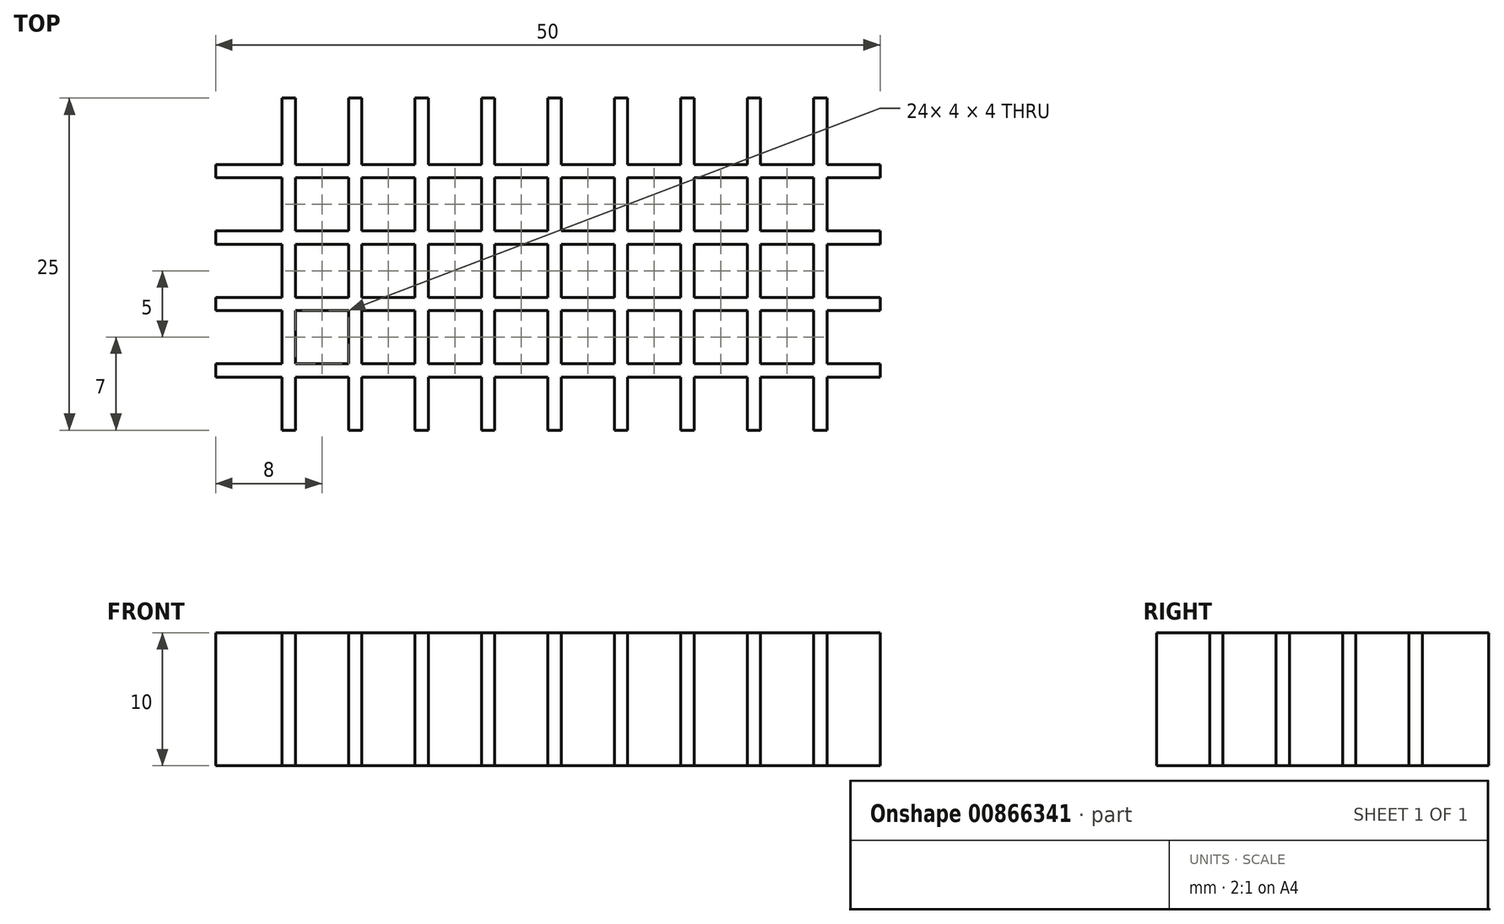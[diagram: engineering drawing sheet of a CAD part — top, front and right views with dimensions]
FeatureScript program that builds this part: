
annotation { "Feature Type Name" : "Feature", "Feature Type Description" : "" }
export const myFeature = defineFeature(function(context is Context, id is Id, definition is map)
    precondition{}
    {
        {
            var Q0;
            Q0=qCreatedBy(makeId("Top.planeOp"),FACE);
            var sketch = newSketch(context, id + "F0", { "sketchPlane" : qUnion([Q0])});
            skLineSegment(sketch, "E0.bottom", {"start": v(0, 0) * mm, "end": v(50, 0) * mm, "construction": true});
            skLineSegment(sketch, "E0.top", {"start": v(0, 25) * mm, "end": v(50, 25) * mm, "construction": true});
            skLineSegment(sketch, "E0.left", {"start": v(0, 0) * mm, "end": v(0, 4) * mm, "construction": true});
            skLineSegment(sketch, "E0.right", {"start": v(50, 0) * mm, "end": v(50, 25) * mm, "construction": true});
            skLineSegment(sketch, "E1", {"start": v(0, 0) * mm, "end": v(0, 25) * mm});
            skLineSegment(sketch, "E2", {"start": v(0, 25) * mm, "end": v(1, 25) * mm});
            skLineSegment(sketch, "E3", {"start": v(1, 24) * mm, "end": v(1, 20) * mm});
            skLineSegment(sketch, "E4", {"start": v(1, 0) * mm, "end": v(0, 0) * mm});
            skLineSegment(sketch, "E5.1.0.0", {"start": v(5, 0) * mm, "end": v(5, 4) * mm});
            skLineSegment(sketch, "E5.1.0.1", {"start": v(6, 24) * mm, "end": v(6, 20) * mm});
            skLineSegment(sketch, "E5.1.0.2", {"start": v(6, 0) * mm, "end": v(5, 0) * mm});
            skLineSegment(sketch, "E5.1.0.3", {"start": v(5, 25) * mm, "end": v(6, 25) * mm});
            skLineSegment(sketch, "E5.2.0.0", {"start": v(10, 0) * mm, "end": v(10, 4) * mm});
            skLineSegment(sketch, "E5.2.0.1", {"start": v(11, 24) * mm, "end": v(11, 20) * mm});
            skLineSegment(sketch, "E5.2.0.2", {"start": v(11, 0) * mm, "end": v(10, 0) * mm});
            skLineSegment(sketch, "E5.2.0.3", {"start": v(10, 25) * mm, "end": v(11, 25) * mm});
            skLineSegment(sketch, "E5.3.0.0", {"start": v(15, 0) * mm, "end": v(15, 4) * mm});
            skLineSegment(sketch, "E5.3.0.1", {"start": v(16, 24) * mm, "end": v(16, 20) * mm});
            skLineSegment(sketch, "E5.3.0.2", {"start": v(16, 0) * mm, "end": v(15, 0) * mm});
            skLineSegment(sketch, "E5.3.0.3", {"start": v(15, 25) * mm, "end": v(16, 25) * mm});
            skLineSegment(sketch, "E5.4.0.0", {"start": v(20, 0) * mm, "end": v(20, 4) * mm});
            skLineSegment(sketch, "E5.4.0.1", {"start": v(21, 24) * mm, "end": v(21, 20) * mm});
            skLineSegment(sketch, "E5.4.0.2", {"start": v(21, 0) * mm, "end": v(20, 0) * mm});
            skLineSegment(sketch, "E5.4.0.3", {"start": v(20, 25) * mm, "end": v(21, 25) * mm});
            skLineSegment(sketch, "E5.5.0.0", {"start": v(25, 0) * mm, "end": v(25, 4) * mm});
            skLineSegment(sketch, "E5.5.0.1", {"start": v(26, 24) * mm, "end": v(26, 20) * mm});
            skLineSegment(sketch, "E5.5.0.2", {"start": v(26, 0) * mm, "end": v(25, 0) * mm});
            skLineSegment(sketch, "E5.5.0.3", {"start": v(25, 25) * mm, "end": v(26, 25) * mm});
            skLineSegment(sketch, "E5.6.0.0", {"start": v(30, 0) * mm, "end": v(30, 4) * mm});
            skLineSegment(sketch, "E5.6.0.1", {"start": v(31, 24) * mm, "end": v(31, 20) * mm});
            skLineSegment(sketch, "E5.6.0.2", {"start": v(31, 0) * mm, "end": v(30, 0) * mm});
            skLineSegment(sketch, "E5.6.0.3", {"start": v(30, 25) * mm, "end": v(31, 25) * mm});
            skLineSegment(sketch, "E5.7.0.0", {"start": v(35, 0) * mm, "end": v(35, 4) * mm});
            skLineSegment(sketch, "E5.7.0.1", {"start": v(36, 24) * mm, "end": v(36, 20) * mm});
            skLineSegment(sketch, "E5.7.0.2", {"start": v(36, 0) * mm, "end": v(35, 0) * mm});
            skLineSegment(sketch, "E5.7.0.3", {"start": v(35, 25) * mm, "end": v(36, 25) * mm});
            skLineSegment(sketch, "E5.8.0.0", {"start": v(40, 0) * mm, "end": v(40, 4) * mm});
            skLineSegment(sketch, "E5.8.0.1", {"start": v(41, 24) * mm, "end": v(41, 20) * mm});
            skLineSegment(sketch, "E5.8.0.2", {"start": v(41, 0) * mm, "end": v(40, 0) * mm});
            skLineSegment(sketch, "E5.8.0.3", {"start": v(40, 25) * mm, "end": v(41, 25) * mm});
            skLineSegment(sketch, "E5.9.0.0", {"start": v(45, 0) * mm, "end": v(45, 4) * mm});
            skLineSegment(sketch, "E5.9.0.1", {"start": v(46, 24) * mm, "end": v(46, 20) * mm});
            skLineSegment(sketch, "E5.9.0.2", {"start": v(46, 0) * mm, "end": v(45, 0) * mm});
            skLineSegment(sketch, "E5.9.0.3", {"start": v(45, 25) * mm, "end": v(46, 25) * mm});
            skLineSegment(sketch, "E5.direction1", {"start": v(0, 0) * mm, "end": v(5, 0) * mm, "construction": true});
            skLineSegment(sketch, "E6", {"start": v(0, 25) * mm, "end": v(50, 25) * mm});
            skLineSegment(sketch, "E7", {"start": v(50, 25) * mm, "end": v(50, 24) * mm});
            skLineSegment(sketch, "E8", {"start": v(50, 24) * mm, "end": v(46, 24) * mm});
            skLineSegment(sketch, "E9", {"start": v(0, 24) * mm, "end": v(0, 25) * mm});
            skLineSegment(sketch, "E10.1.0.0", {"start": v(50, 19) * mm, "end": v(46, 19) * mm});
            skLineSegment(sketch, "E10.1.0.1", {"start": v(1, 20) * mm, "end": v(5, 20) * mm});
            skLineSegment(sketch, "E10.1.0.2", {"start": v(0, 19) * mm, "end": v(0, 20) * mm});
            skLineSegment(sketch, "E10.1.0.3", {"start": v(50, 20) * mm, "end": v(50, 19) * mm});
            skLineSegment(sketch, "E10.2.0.0", {"start": v(50, 14) * mm, "end": v(46, 14) * mm});
            skLineSegment(sketch, "E10.2.0.1", {"start": v(1, 15) * mm, "end": v(5, 15) * mm});
            skLineSegment(sketch, "E10.2.0.2", {"start": v(0, 14) * mm, "end": v(0, 15) * mm});
            skLineSegment(sketch, "E10.2.0.3", {"start": v(50, 15) * mm, "end": v(50, 14) * mm});
            skLineSegment(sketch, "E10.3.0.0", {"start": v(50, 9) * mm, "end": v(46, 9) * mm});
            skLineSegment(sketch, "E10.3.0.1", {"start": v(1, 10) * mm, "end": v(5, 10) * mm});
            skLineSegment(sketch, "E10.3.0.2", {"start": v(0, 9) * mm, "end": v(0, 10) * mm});
            skLineSegment(sketch, "E10.3.0.3", {"start": v(50, 10) * mm, "end": v(50, 9) * mm});
            skLineSegment(sketch, "E10.4.0.0", {"start": v(50, 4) * mm, "end": v(46, 4) * mm});
            skLineSegment(sketch, "E10.4.0.1", {"start": v(1, 5) * mm, "end": v(5, 5) * mm});
            skLineSegment(sketch, "E10.4.0.2", {"start": v(0, 4) * mm, "end": v(0, 5) * mm});
            skLineSegment(sketch, "E10.4.0.3", {"start": v(50, 5) * mm, "end": v(50, 4) * mm});
            skLineSegment(sketch, "E10.direction1", {"start": v(0, 24) * mm, "end": v(0, 19) * mm, "construction": true});
            skLineSegment(sketch, "E11.trimOffspring", {"start": v(5, 5) * mm, "end": v(5, 9) * mm});
            skLineSegment(sketch, "E12.trimOffspring", {"start": v(6, 5) * mm, "end": v(10, 5) * mm});
            skLineSegment(sketch, "E13.trimOffspring", {"start": v(6, 4) * mm, "end": v(6, 0) * mm});
            skLineSegment(sketch, "E14.trimOffspring", {"start": v(5, 4) * mm, "end": v(1, 4) * mm});
            skLineSegment(sketch, "E15.trimOffspring", {"start": v(1, 4) * mm, "end": v(1, 0) * mm});
            skPoint(sketch, "E16.orphan", {"position": v(0, 5) * mm});
            skPoint(sketch, "E17.orphan", {"position": v(0, 10) * mm});
            skPoint(sketch, "E18.orphan", {"position": v(0, 15) * mm});
            skPoint(sketch, "E19.orphan", {"position": v(0, 20) * mm});
            skLineSegment(sketch, "E20.trimOffspring", {"start": v(46, 20) * mm, "end": v(50, 20) * mm});
            skLineSegment(sketch, "E21.trimOffspring", {"start": v(45, 19) * mm, "end": v(41, 19) * mm});
            skLineSegment(sketch, "E22.trimOffspring", {"start": v(45, 20) * mm, "end": v(45, 24) * mm});
            skLineSegment(sketch, "E23.trimOffspring", {"start": v(46, 19) * mm, "end": v(46, 15) * mm});
            skLineSegment(sketch, "E24.trimOffspring", {"start": v(46, 15) * mm, "end": v(50, 15) * mm});
            skLineSegment(sketch, "E25.trimOffspring", {"start": v(45, 14) * mm, "end": v(41, 14) * mm});
            skLineSegment(sketch, "E26.trimOffspring", {"start": v(45, 15) * mm, "end": v(45, 19) * mm});
            skLineSegment(sketch, "E27.trimOffspring", {"start": v(46, 14) * mm, "end": v(46, 10) * mm});
            skLineSegment(sketch, "E28.trimOffspring", {"start": v(46, 10) * mm, "end": v(50, 10) * mm});
            skLineSegment(sketch, "E29.trimOffspring", {"start": v(46, 9) * mm, "end": v(46, 5) * mm});
            skLineSegment(sketch, "E30.trimOffspring", {"start": v(45, 9) * mm, "end": v(41, 9) * mm});
            skLineSegment(sketch, "E31.trimOffspring", {"start": v(45, 10) * mm, "end": v(45, 14) * mm});
            skLineSegment(sketch, "E32.trimOffspring", {"start": v(46, 5) * mm, "end": v(50, 5) * mm});
            skLineSegment(sketch, "E33.trimOffspring", {"start": v(46, 4) * mm, "end": v(46, 0) * mm});
            skLineSegment(sketch, "E34.trimOffspring", {"start": v(45, 4) * mm, "end": v(41, 4) * mm});
            skLineSegment(sketch, "E35.trimOffspring", {"start": v(45, 5) * mm, "end": v(45, 9) * mm});
            skLineSegment(sketch, "E36.trimOffspring", {"start": v(40, 5) * mm, "end": v(40, 9) * mm});
            skLineSegment(sketch, "E37.trimOffspring", {"start": v(41, 5) * mm, "end": v(45, 5) * mm});
            skLineSegment(sketch, "E38.trimOffspring", {"start": v(41, 4) * mm, "end": v(41, 0) * mm});
            skLineSegment(sketch, "E39.trimOffspring", {"start": v(40, 4) * mm, "end": v(36, 4) * mm});
            skLineSegment(sketch, "E40.trimOffspring", {"start": v(36, 5) * mm, "end": v(40, 5) * mm});
            skLineSegment(sketch, "E41.trimOffspring", {"start": v(36, 4) * mm, "end": v(36, 0) * mm});
            skLineSegment(sketch, "E42.trimOffspring", {"start": v(35, 4) * mm, "end": v(31, 4) * mm});
            skLineSegment(sketch, "E43.trimOffspring", {"start": v(35, 5) * mm, "end": v(35, 9) * mm});
            skLineSegment(sketch, "E44.trimOffspring", {"start": v(35, 9) * mm, "end": v(31, 9) * mm});
            skLineSegment(sketch, "E45.trimOffspring", {"start": v(35, 10) * mm, "end": v(35, 14) * mm});
            skLineSegment(sketch, "E46.trimOffspring", {"start": v(36, 10) * mm, "end": v(40, 10) * mm});
            skLineSegment(sketch, "E47.trimOffspring", {"start": v(36, 9) * mm, "end": v(36, 5) * mm});
            skLineSegment(sketch, "E48.trimOffspring", {"start": v(40, 10) * mm, "end": v(40, 14) * mm});
            skLineSegment(sketch, "E49.trimOffspring", {"start": v(41, 10) * mm, "end": v(45, 10) * mm});
            skLineSegment(sketch, "E50.trimOffspring", {"start": v(41, 9) * mm, "end": v(41, 5) * mm});
            skLineSegment(sketch, "E51.trimOffspring", {"start": v(40, 9) * mm, "end": v(36, 9) * mm});
            skLineSegment(sketch, "E52.trimOffspring", {"start": v(40, 14) * mm, "end": v(36, 14) * mm});
            skLineSegment(sketch, "E53.trimOffspring", {"start": v(41, 15) * mm, "end": v(45, 15) * mm});
            skLineSegment(sketch, "E54.trimOffspring", {"start": v(40, 15) * mm, "end": v(40, 19) * mm});
            skLineSegment(sketch, "E55.trimOffspring", {"start": v(41, 14) * mm, "end": v(41, 10) * mm});
            skLineSegment(sketch, "E56.trimOffspring", {"start": v(40, 19) * mm, "end": v(36, 19) * mm});
            skLineSegment(sketch, "E57.trimOffspring", {"start": v(41, 20) * mm, "end": v(45, 20) * mm});
            skLineSegment(sketch, "E58.trimOffspring", {"start": v(40, 20) * mm, "end": v(40, 24) * mm});
            skLineSegment(sketch, "E59.trimOffspring", {"start": v(41, 19) * mm, "end": v(41, 15) * mm});
            skLineSegment(sketch, "E60.trimOffspring", {"start": v(35, 24) * mm, "end": v(31, 24) * mm});
            skLineSegment(sketch, "E61.trimOffspring", {"start": v(40, 24) * mm, "end": v(36, 24) * mm});
            skLineSegment(sketch, "E62.trimOffspring", {"start": v(36, 20) * mm, "end": v(40, 20) * mm});
            skLineSegment(sketch, "E63.trimOffspring", {"start": v(35, 20) * mm, "end": v(35, 24) * mm});
            skLineSegment(sketch, "E64.trimOffspring", {"start": v(35, 19) * mm, "end": v(31, 19) * mm});
            skLineSegment(sketch, "E65.trimOffspring", {"start": v(36, 19) * mm, "end": v(36, 15) * mm});
            skLineSegment(sketch, "E66.trimOffspring", {"start": v(5, 24) * mm, "end": v(1, 24) * mm});
            skLineSegment(sketch, "E67.trimOffspring", {"start": v(10, 24) * mm, "end": v(6, 24) * mm});
            skLineSegment(sketch, "E68.trimOffspring", {"start": v(15, 24) * mm, "end": v(11, 24) * mm});
            skLineSegment(sketch, "E69.trimOffspring", {"start": v(20, 24) * mm, "end": v(16, 24) * mm});
            skLineSegment(sketch, "E70.trimOffspring", {"start": v(25, 24) * mm, "end": v(21, 24) * mm});
            skLineSegment(sketch, "E71.trimOffspring", {"start": v(30, 24) * mm, "end": v(26, 24) * mm});
            skLineSegment(sketch, "E72.trimOffspring", {"start": v(31, 20) * mm, "end": v(35, 20) * mm});
            skLineSegment(sketch, "E73.trimOffspring", {"start": v(30, 20) * mm, "end": v(30, 24) * mm});
            skLineSegment(sketch, "E74.trimOffspring", {"start": v(30, 19) * mm, "end": v(26, 19) * mm});
            skLineSegment(sketch, "E75.trimOffspring", {"start": v(31, 19) * mm, "end": v(31, 15) * mm});
            skLineSegment(sketch, "E76.trimOffspring", {"start": v(26, 19) * mm, "end": v(26, 15) * mm});
            skLineSegment(sketch, "E77.trimOffspring", {"start": v(26, 20) * mm, "end": v(30, 20) * mm});
            skLineSegment(sketch, "E78.trimOffspring", {"start": v(25, 20) * mm, "end": v(25, 24) * mm});
            skLineSegment(sketch, "E79.trimOffspring", {"start": v(25, 19) * mm, "end": v(21, 19) * mm});
            skLineSegment(sketch, "E80.trimOffspring", {"start": v(21, 19) * mm, "end": v(21, 15) * mm});
            skLineSegment(sketch, "E81.trimOffspring", {"start": v(21, 20) * mm, "end": v(25, 20) * mm});
            skLineSegment(sketch, "E82.trimOffspring", {"start": v(20, 20) * mm, "end": v(20, 24) * mm});
            skLineSegment(sketch, "E83.trimOffspring", {"start": v(20, 19) * mm, "end": v(16, 19) * mm});
            skLineSegment(sketch, "E84.trimOffspring", {"start": v(16, 19) * mm, "end": v(16, 15) * mm});
            skLineSegment(sketch, "E85.trimOffspring", {"start": v(16, 20) * mm, "end": v(20, 20) * mm});
            skLineSegment(sketch, "E86.trimOffspring", {"start": v(15, 20) * mm, "end": v(15, 24) * mm});
            skLineSegment(sketch, "E87.trimOffspring", {"start": v(15, 19) * mm, "end": v(11, 19) * mm});
            skLineSegment(sketch, "E88.trimOffspring", {"start": v(11, 19) * mm, "end": v(11, 15) * mm});
            skLineSegment(sketch, "E89.trimOffspring", {"start": v(11, 20) * mm, "end": v(15, 20) * mm});
            skLineSegment(sketch, "E90.trimOffspring", {"start": v(10, 20) * mm, "end": v(10, 24) * mm});
            skLineSegment(sketch, "E91.trimOffspring", {"start": v(10, 19) * mm, "end": v(6, 19) * mm});
            skLineSegment(sketch, "E92.trimOffspring", {"start": v(6, 20) * mm, "end": v(10, 20) * mm});
            skLineSegment(sketch, "E93.trimOffspring", {"start": v(5, 19) * mm, "end": v(1, 19) * mm});
            skLineSegment(sketch, "E94.trimOffspring", {"start": v(5, 20) * mm, "end": v(5, 24) * mm});
            skLineSegment(sketch, "E95.trimOffspring", {"start": v(6, 19) * mm, "end": v(6, 15) * mm});
            skLineSegment(sketch, "E96.trimOffspring", {"start": v(6, 15) * mm, "end": v(10, 15) * mm});
            skLineSegment(sketch, "E97.trimOffspring", {"start": v(5, 15) * mm, "end": v(5, 19) * mm});
            skLineSegment(sketch, "E98.trimOffspring", {"start": v(5, 14) * mm, "end": v(1, 14) * mm});
            skLineSegment(sketch, "E99.trimOffspring", {"start": v(6, 14) * mm, "end": v(6, 10) * mm});
            skLineSegment(sketch, "E100.trimOffspring", {"start": v(6, 10) * mm, "end": v(10, 10) * mm});
            skLineSegment(sketch, "E101.trimOffspring", {"start": v(5, 10) * mm, "end": v(5, 14) * mm});
            skLineSegment(sketch, "E102.trimOffspring", {"start": v(5, 9) * mm, "end": v(1, 9) * mm});
            skLineSegment(sketch, "E103.trimOffspring", {"start": v(6, 9) * mm, "end": v(6, 5) * mm});
            skLineSegment(sketch, "E104.trimOffspring", {"start": v(10, 5) * mm, "end": v(10, 9) * mm});
            skLineSegment(sketch, "E105.trimOffspring", {"start": v(11, 5) * mm, "end": v(15, 5) * mm});
            skLineSegment(sketch, "E106.trimOffspring", {"start": v(10, 4) * mm, "end": v(6, 4) * mm});
            skLineSegment(sketch, "E107.trimOffspring", {"start": v(11, 4) * mm, "end": v(11, 0) * mm});
            skLineSegment(sketch, "E108.trimOffspring", {"start": v(10, 9) * mm, "end": v(6, 9) * mm});
            skLineSegment(sketch, "E109.trimOffspring", {"start": v(11, 10) * mm, "end": v(15, 10) * mm});
            skLineSegment(sketch, "E110.trimOffspring", {"start": v(10, 10) * mm, "end": v(10, 14) * mm});
            skLineSegment(sketch, "E111.trimOffspring", {"start": v(11, 9) * mm, "end": v(11, 5) * mm});
            skLineSegment(sketch, "E112.trimOffspring", {"start": v(16, 5) * mm, "end": v(20, 5) * mm});
            skLineSegment(sketch, "E113.trimOffspring", {"start": v(15, 5) * mm, "end": v(15, 9) * mm});
            skLineSegment(sketch, "E114.trimOffspring", {"start": v(15, 4) * mm, "end": v(11, 4) * mm});
            skLineSegment(sketch, "E115.trimOffspring", {"start": v(16, 4) * mm, "end": v(16, 0) * mm});
            skLineSegment(sketch, "E116.trimOffspring", {"start": v(15, 9) * mm, "end": v(11, 9) * mm});
            skLineSegment(sketch, "E117.trimOffspring", {"start": v(15, 10) * mm, "end": v(15, 14) * mm});
            skLineSegment(sketch, "E118.trimOffspring", {"start": v(16, 10) * mm, "end": v(20, 10) * mm});
            skLineSegment(sketch, "E119.trimOffspring", {"start": v(16, 9) * mm, "end": v(16, 5) * mm});
            skLineSegment(sketch, "E120.trimOffspring", {"start": v(15, 14) * mm, "end": v(11, 14) * mm});
            skLineSegment(sketch, "E121.trimOffspring", {"start": v(16, 15) * mm, "end": v(20, 15) * mm});
            skLineSegment(sketch, "E122.trimOffspring", {"start": v(15, 15) * mm, "end": v(15, 19) * mm});
            skLineSegment(sketch, "E123.trimOffspring", {"start": v(16, 14) * mm, "end": v(16, 10) * mm});
            skLineSegment(sketch, "E124.trimOffspring", {"start": v(11, 14) * mm, "end": v(11, 10) * mm});
            skLineSegment(sketch, "E125.trimOffspring", {"start": v(11, 15) * mm, "end": v(15, 15) * mm});
            skLineSegment(sketch, "E126.trimOffspring", {"start": v(10, 14) * mm, "end": v(6, 14) * mm});
            skLineSegment(sketch, "E127.trimOffspring", {"start": v(10, 15) * mm, "end": v(10, 19) * mm});
            skLineSegment(sketch, "E128.trimOffspring", {"start": v(20, 15) * mm, "end": v(20, 19) * mm});
            skLineSegment(sketch, "E129.trimOffspring", {"start": v(21, 15) * mm, "end": v(25, 15) * mm});
            skLineSegment(sketch, "E130.trimOffspring", {"start": v(21, 14) * mm, "end": v(21, 10) * mm});
            skLineSegment(sketch, "E131.trimOffspring", {"start": v(20, 14) * mm, "end": v(16, 14) * mm});
            skLineSegment(sketch, "E132.trimOffspring", {"start": v(21, 10) * mm, "end": v(25, 10) * mm});
            skLineSegment(sketch, "E133.trimOffspring", {"start": v(20, 10) * mm, "end": v(20, 14) * mm});
            skLineSegment(sketch, "E134.trimOffspring", {"start": v(20, 9) * mm, "end": v(16, 9) * mm});
            skLineSegment(sketch, "E135.trimOffspring", {"start": v(21, 9) * mm, "end": v(21, 5) * mm});
            skLineSegment(sketch, "E136.trimOffspring", {"start": v(25, 10) * mm, "end": v(25, 14) * mm});
            skLineSegment(sketch, "E137.trimOffspring", {"start": v(26, 10) * mm, "end": v(30, 10) * mm});
            skLineSegment(sketch, "E138.trimOffspring", {"start": v(26, 9) * mm, "end": v(26, 5) * mm});
            skLineSegment(sketch, "E139.trimOffspring", {"start": v(25, 9) * mm, "end": v(21, 9) * mm});
            skLineSegment(sketch, "E140.trimOffspring", {"start": v(25, 14) * mm, "end": v(21, 14) * mm});
            skLineSegment(sketch, "E141.trimOffspring", {"start": v(25, 15) * mm, "end": v(25, 19) * mm});
            skLineSegment(sketch, "E142.trimOffspring", {"start": v(26, 15) * mm, "end": v(30, 15) * mm});
            skLineSegment(sketch, "E143.trimOffspring", {"start": v(26, 14) * mm, "end": v(26, 10) * mm});
            skLineSegment(sketch, "E144.trimOffspring", {"start": v(30, 15) * mm, "end": v(30, 19) * mm});
            skLineSegment(sketch, "E145.trimOffspring", {"start": v(31, 14) * mm, "end": v(31, 10) * mm});
            skLineSegment(sketch, "E146.trimOffspring", {"start": v(30, 14) * mm, "end": v(26, 14) * mm});
            skLineSegment(sketch, "E147.trimOffspring", {"start": v(31, 15) * mm, "end": v(35, 15) * mm});
            skLineSegment(sketch, "E148.trimOffspring", {"start": v(31, 10) * mm, "end": v(35, 10) * mm});
            skLineSegment(sketch, "E149.trimOffspring", {"start": v(31, 9) * mm, "end": v(31, 5) * mm});
            skLineSegment(sketch, "E150.trimOffspring", {"start": v(30, 9) * mm, "end": v(26, 9) * mm});
            skLineSegment(sketch, "E151.trimOffspring", {"start": v(30, 10) * mm, "end": v(30, 14) * mm});
            skLineSegment(sketch, "E152.trimOffspring", {"start": v(0, 9) * mm, "end": v(0, 15) * mm, "construction": true});
            skLineSegment(sketch, "E153.trimOffspring", {"start": v(0, 19) * mm, "end": v(0, 25) * mm, "construction": true});
            skLineSegment(sketch, "E154", {"start": v(1, 10) * mm, "end": v(0, 10) * mm});
            skLineSegment(sketch, "E155", {"start": v(0, 9) * mm, "end": v(1, 9) * mm});
            skLineSegment(sketch, "E156", {"start": v(0, 5) * mm, "end": v(1, 5) * mm});
            skLineSegment(sketch, "E157", {"start": v(0, 4) * mm, "end": v(1, 4) * mm});
            skLineSegment(sketch, "E158", {"start": v(0, 20) * mm, "end": v(1, 20) * mm});
            skLineSegment(sketch, "E159", {"start": v(0, 19) * mm, "end": v(1, 19) * mm});
            skLineSegment(sketch, "E160", {"start": v(0, 15) * mm, "end": v(1, 15) * mm});
            skLineSegment(sketch, "E161", {"start": v(0, 14) * mm, "end": v(1, 14) * mm});
            skLineSegment(sketch, "E162", {"start": v(0, 24) * mm, "end": v(1, 24) * mm});
            skLineSegment(sketch, "E163", {"start": v(1, 24) * mm, "end": v(1, 25) * mm});
            skLineSegment(sketch, "E164", {"start": v(5, 24) * mm, "end": v(5, 25) * mm});
            skLineSegment(sketch, "E165", {"start": v(6, 24) * mm, "end": v(6, 25) * mm});
            skLineSegment(sketch, "E166", {"start": v(10, 24) * mm, "end": v(10, 25) * mm});
            skLineSegment(sketch, "E167", {"start": v(11, 25) * mm, "end": v(11, 24) * mm});
            skLineSegment(sketch, "E168", {"start": v(15, 25) * mm, "end": v(15, 24) * mm});
            skLineSegment(sketch, "E169", {"start": v(16, 25) * mm, "end": v(16, 24) * mm});
            skLineSegment(sketch, "E170", {"start": v(20, 25) * mm, "end": v(20, 24) * mm});
            skLineSegment(sketch, "E171", {"start": v(21, 25) * mm, "end": v(21, 24) * mm});
            skLineSegment(sketch, "E172", {"start": v(25, 25) * mm, "end": v(25, 24) * mm});
            skLineSegment(sketch, "E173", {"start": v(26, 25) * mm, "end": v(26, 24) * mm});
            skLineSegment(sketch, "E174", {"start": v(30, 25) * mm, "end": v(30, 24) * mm});
            skLineSegment(sketch, "E175", {"start": v(31, 25) * mm, "end": v(31, 24) * mm});
            skLineSegment(sketch, "E176", {"start": v(35, 25) * mm, "end": v(35, 24) * mm});
            skLineSegment(sketch, "E177", {"start": v(36, 25) * mm, "end": v(36, 24) * mm});
            skLineSegment(sketch, "E178", {"start": v(40, 25) * mm, "end": v(40, 24) * mm});
            skLineSegment(sketch, "E179", {"start": v(41, 25) * mm, "end": v(41, 24) * mm});
            skLineSegment(sketch, "E180", {"start": v(45, 25) * mm, "end": v(45, 24) * mm});
            skLineSegment(sketch, "E181", {"start": v(46, 25) * mm, "end": v(46, 24) * mm});
            skLineSegment(sketch, "E182.trimOffspring", {"start": v(45, 24) * mm, "end": v(41, 24) * mm});
            skLineSegment(sketch, "E183.trimOffspring", {"start": v(1, 19) * mm, "end": v(1, 15) * mm});
            skLineSegment(sketch, "E184.trimOffspring", {"start": v(1, 14) * mm, "end": v(1, 10) * mm});
            skLineSegment(sketch, "E185.trimOffspring", {"start": v(1, 9) * mm, "end": v(1, 5) * mm});
            skLineSegment(sketch, "E186.trimOffspring", {"start": v(21, 4) * mm, "end": v(21, 0) * mm});
            skLineSegment(sketch, "E187.trimOffspring", {"start": v(20, 5) * mm, "end": v(20, 9) * mm});
            skLineSegment(sketch, "E188.trimOffspring", {"start": v(21, 5) * mm, "end": v(25, 5) * mm});
            skLineSegment(sketch, "E189.trimOffspring", {"start": v(20, 4) * mm, "end": v(16, 4) * mm});
            skLineSegment(sketch, "E190.trimOffspring", {"start": v(25, 5) * mm, "end": v(25, 9) * mm});
            skLineSegment(sketch, "E191.trimOffspring", {"start": v(26, 4) * mm, "end": v(26, 0) * mm});
            skLineSegment(sketch, "E192.trimOffspring", {"start": v(26, 5) * mm, "end": v(30, 5) * mm});
            skLineSegment(sketch, "E193.trimOffspring", {"start": v(25, 4) * mm, "end": v(21, 4) * mm});
            skLineSegment(sketch, "E194.trimOffspring", {"start": v(30, 5) * mm, "end": v(30, 9) * mm});
            skLineSegment(sketch, "E195.trimOffspring", {"start": v(31, 5) * mm, "end": v(35, 5) * mm});
            skLineSegment(sketch, "E196.trimOffspring", {"start": v(31, 4) * mm, "end": v(31, 0) * mm});
            skLineSegment(sketch, "E197.trimOffspring", {"start": v(30, 4) * mm, "end": v(26, 4) * mm});
            skLineSegment(sketch, "E198.trimOffspring", {"start": v(36, 15) * mm, "end": v(40, 15) * mm});
            skLineSegment(sketch, "E199.trimOffspring", {"start": v(35, 15) * mm, "end": v(35, 19) * mm});
            skLineSegment(sketch, "E200.trimOffspring", {"start": v(35, 14) * mm, "end": v(31, 14) * mm});
            skLineSegment(sketch, "E201.trimOffspring", {"start": v(36, 14) * mm, "end": v(36, 10) * mm});
            skSolve(sketch);
        }
        {
            var Q0;
            Q0=makeQuery(id+"F0.imprint","IMPRINT",FACE,{"disambiguationData":[TD([[makeQuery(id+"F0.imprint","IMPRINT",EDGE,{"derivedFrom":sQuery(id+"F0.wireOp",EDGE,"E5.1.0.0")}),-1.0]])]});
            extrude(context, id + "F1", {"entities" : qUnion([Q0]), "depth" : 10 * mm, "offsetDistance" : 25 * mm});
        }
    });
